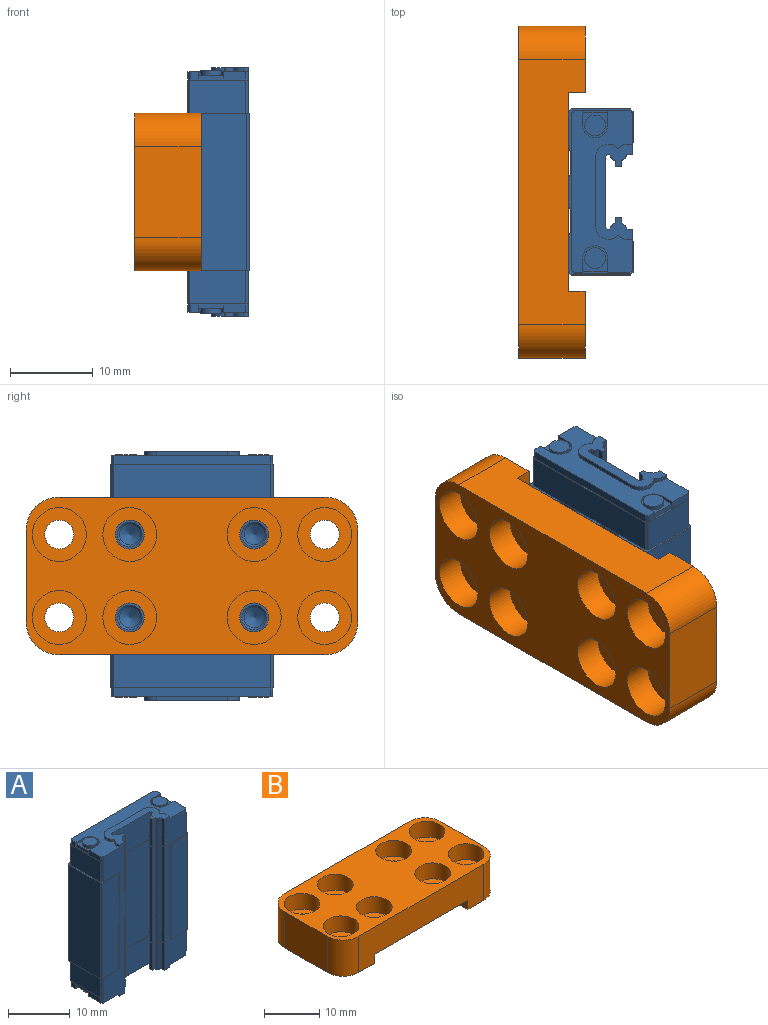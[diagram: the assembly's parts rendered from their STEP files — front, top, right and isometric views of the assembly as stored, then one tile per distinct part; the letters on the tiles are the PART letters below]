
ASSEMBLY  parts=2 mates=1
PART A: 240 faces, bbox 20x7.8x30 mm
  f0: cone r=0mm half-angle=60deg, axis (0,1,0), area 5.5mm2, adj f8
  f1: cone r=0mm half-angle=60deg, axis (0,1,0), area 5.5mm2, adj f9
  f2: cone r=0mm half-angle=60deg, axis (0,1,0), area 5.5mm2, adj f10
  f3: cone r=0mm half-angle=60deg, axis (0,1,0), area 5.5mm2, adj f11
  f4: plane 2.5x2.5mm, normal (0,0,1), area 4.9mm2, adj f12
  f5: plane 2.5x2.5mm, normal (0,0,1), area 4.9mm2, adj f13
  f6: plane 19x0.26mm, normal (1,0,0), area 4.9mm2, adj f21,f22,f91,f92
  f7: plane 19x0.26mm, normal (-1,0,0), area 4.9mm2, adj f24,f25,f91,f92
  f8: cylinder r=1.23mm len=5.73mm, axis (0,-1,0), area 44.3mm2, adj f0,f31
  f9: cylinder r=1.23mm len=5.73mm, axis (0,-1,0), area 44.3mm2, adj f1,f32
  f10: cylinder r=1.23mm len=5.73mm, axis (0,-1,0), area 44.3mm2, adj f2,f33
  f11: cylinder r=1.23mm len=5.73mm, axis (0,-1,0), area 44.3mm2, adj f3,f34
  f12: cylinder r=1.25mm len=2.5mm, axis (0,0,-1), area 3.9mm2, adj f4,f35
  f13: cylinder r=1.25mm len=2.5mm, axis (0,0,-1), area 3.9mm2, adj f5,f37
  f14: plane 2.5x2.5mm, normal (0,0,-1), area 4.9mm2, adj f89
  f15: plane 2.5x2.5mm, normal (0,0,-1), area 4.9mm2, adj f90
  f16: cylinder r=1.1mm len=19mm, axis (0,0,-1), area 13.7mm2, adj f17,f88,f91,f92
  f17: plane 19x0.66mm, normal (0,-1,0), area 12.4mm2, adj f16,f18,f91,f92
  f18: plane 19x0.7mm, normal (1,0,0), area 13.3mm2, adj f17,f19,f91,f92
  f19: plane 19x0.66mm, normal (0,1,0), area 12.4mm2, adj f18,f20,f91,f92
  f20: cylinder r=1.1mm len=19mm, axis (0,0,-1), area 13.7mm2, adj f19,f21,f91,f92
  f21: plane 19x0.28mm, normal (0.5,0.87,0), area 6.1mm2, adj f6,f20,f91,f92
  f22: plane 19x0.2mm, normal (0.71,-0.71,0), area 5.4mm2, adj f6,f23,f91,f92
  f23: plane 19x8.6mm, normal (0,-1,0), area 163.4mm2, adj f22,f24,f91,f92
  f24: plane 19x0.2mm, normal (-0.71,-0.71,0), area 5.4mm2, adj f7,f23,f91,f92
  f25: plane 19x0.28mm, normal (-0.5,0.87,0), area 6.1mm2, adj f7,f26,f91,f92
  f26: cylinder r=1.1mm len=19mm, axis (0,0,-1), area 13.7mm2, adj f25,f27,f91,f92
  f27: plane 19x0.66mm, normal (0,1,0), area 12.4mm2, adj f26,f28,f91,f92
  f28: plane 19x0.7mm, normal (-1,0,0), area 13.3mm2, adj f27,f29,f91,f92
  f29: plane 19x0.66mm, normal (0,-1,0), area 12.4mm2, adj f28,f30,f91,f92
  f30: cylinder r=1.1mm len=19mm, axis (0,0,-1), area 13.7mm2, adj f29,f91,f92,f93
  f31: cone r=0mm half-angle=45deg, axis (0,1,0), area 3.3mm2, adj f8,f106
  f32: cone r=0mm half-angle=45deg, axis (0,1,0), area 3.3mm2, adj f9,f106
  f33: cone r=0mm half-angle=45deg, axis (0,1,0), area 3.3mm2, adj f10,f114
  f34: cone r=0mm half-angle=45deg, axis (0,1,0), area 3.3mm2, adj f11,f114
  f35: plane 3.05x3mm, normal (0,0,1), area 3.3mm2, adj f12,f36,f123,f124,f125
  f36: plane 3x0.6mm, normal (1,0,0), area 1.8mm2, adj f35,f121,f123,f125
  f37: plane 3.05x3mm, normal (0,0,1), area 3.3mm2, adj f13,f38,f131,f132,f133,f134
  f38: plane 3x0.6mm, normal (-1,0,0), area 1.8mm2, adj f37,f121,f131,f134
  f39: plane 5.45x0.26mm, normal (1,0,0), area 1.4mm2, adj f142,f143,f159,f187
  f40: plane 5.45x0.26mm, normal (-1,0,0), area 1.4mm2, adj f145,f146,f159,f187
  f41: cylinder r=0.1mm len=0.5mm, axis (0,0,1), area 0.1mm2, adj f152,f153,f185,f187
  f42: plane 0.5x0.15mm, normal (1,0,0), area 0.1mm2, adj f153,f154,f185,f187
  f43: plane 0.5x0.15mm, normal (-1,0,0), area 0.1mm2, adj f156,f157,f185,f187
  f44: cylinder r=0.1mm len=0.5mm, axis (0,0,1), area 0mm2, adj f45,f157,f185,f187
  f45: cylinder r=0.1mm len=0.5mm, axis (0,0,1), area 0mm2, adj f44,f158,f185,f187
  f46: plane 0.71x0.05mm, normal (1,0,0), area 0mm2, adj f47,f92,f159,f215
  f47: plane 0.25x0.12mm, normal (0.45,-0.89,0), area 0mm2, adj f46,f48,f92,f159
  f48: cylinder r=1.05mm len=0.57mm, axis (0,0,-1), area 0mm2, adj f47,f49,f92,f159
  f49: plane 0.64x0.05mm, normal (0,-1,0), area 0mm2, adj f48,f50,f92,f159
  f50: plane 0.6x0.05mm, normal (1,0,0), area 0mm2, adj f49,f51,f92,f159
  f51: plane 0.64x0.05mm, normal (0,1,0), area 0mm2, adj f50,f52,f92,f159
  f52: cylinder r=1.05mm len=0.57mm, axis (0,0,-1), area 0mm2, adj f51,f53,f92,f159
  f53: plane 0.25x0.12mm, normal (0.45,0.89,0), area 0mm2, adj f52,f54,f92,f159
  f54: plane 0.36x0.05mm, normal (1,0,0), area 0mm2, adj f53,f55,f92,f159
  f55: plane 0.2x0.2mm, normal (0.71,-0.71,0), area 0mm2, adj f54,f56,f92,f159
  f56: plane 8.7x0.05mm, normal (0,-1,0), area 0.4mm2, adj f55,f57,f92,f159
  f57: plane 0.2x0.2mm, normal (-0.71,-0.71,0), area 0mm2, adj f56,f58,f92,f159
  f58: plane 0.36x0.05mm, normal (-1,0,0), area 0mm2, adj f57,f59,f92,f159
  f59: plane 0.25x0.12mm, normal (-0.45,0.89,0), area 0mm2, adj f58,f60,f92,f159
  f60: cylinder r=1.05mm len=0.57mm, axis (0,0,-1), area 0mm2, adj f59,f61,f92,f159
  f61: plane 0.64x0.05mm, normal (0,1,0), area 0mm2, adj f60,f62,f92,f159
  f62: plane 0.6x0.05mm, normal (-1,0,0), area 0mm2, adj f61,f63,f92,f159
  f63: plane 0.64x0.05mm, normal (0,-1,0), area 0mm2, adj f62,f64,f92,f159
  f64: cylinder r=1.05mm len=0.57mm, axis (0,0,-1), area 0mm2, adj f63,f65,f92,f159
  f65: plane 0.25x0.12mm, normal (-0.45,-0.89,0), area 0mm2, adj f64,f66,f92,f159
  f66: plane 0.71x0.05mm, normal (-1,0,0), area 0mm2, adj f65,f92,f159,f232
  f67: plane 0.71x0.05mm, normal (-1,0,0), area 0mm2, adj f68,f91,f163,f232
  f68: plane 0.25x0.12mm, normal (-0.45,-0.89,0), area 0mm2, adj f67,f69,f91,f163
  f69: cylinder r=1.05mm len=0.57mm, axis (0,0,1), area 0mm2, adj f68,f70,f91,f163
  f70: plane 0.64x0.05mm, normal (0,-1,0), area 0mm2, adj f69,f71,f91,f163
  f71: plane 0.6x0.05mm, normal (-1,0,0), area 0mm2, adj f70,f72,f91,f163
  f72: plane 0.64x0.05mm, normal (0,1,0), area 0mm2, adj f71,f73,f91,f163
  f73: cylinder r=1.05mm len=0.57mm, axis (0,0,1), area 0mm2, adj f72,f74,f91,f163
  f74: plane 0.25x0.12mm, normal (-0.45,0.89,0), area 0mm2, adj f73,f75,f91,f163
  f75: plane 0.36x0.05mm, normal (-1,0,0), area 0mm2, adj f74,f76,f91,f163
  f76: plane 0.2x0.2mm, normal (-0.71,-0.71,0), area 0mm2, adj f75,f77,f91,f163
  f77: plane 8.7x0.05mm, normal (0,-1,0), area 0.4mm2, adj f76,f78,f91,f163
  f78: plane 0.2x0.2mm, normal (0.71,-0.71,0), area 0mm2, adj f77,f79,f91,f163
  f79: plane 0.36x0.05mm, normal (1,0,0), area 0mm2, adj f78,f80,f91,f163
  f80: plane 0.25x0.12mm, normal (0.45,0.89,0), area 0mm2, adj f79,f81,f91,f163
  f81: cylinder r=1.05mm len=0.57mm, axis (0,0,1), area 0mm2, adj f80,f82,f91,f163
  f82: plane 0.64x0.05mm, normal (0,1,0), area 0mm2, adj f81,f83,f91,f163
  f83: plane 0.6x0.05mm, normal (1,0,0), area 0mm2, adj f82,f84,f91,f163
  f84: plane 0.64x0.05mm, normal (0,-1,0), area 0mm2, adj f83,f85,f91,f163
  f85: cylinder r=1.05mm len=0.57mm, axis (0,0,1), area 0mm2, adj f84,f86,f91,f163
  f86: plane 0.25x0.12mm, normal (0.45,-0.89,0), area 0mm2, adj f85,f87,f91,f163
  f87: plane 0.71x0.05mm, normal (1,0,0), area 0mm2, adj f86,f91,f163,f215
  f88: plane 19x0.28mm, normal (0.5,-0.87,0), area 6.1mm2, adj f16,f91,f92,f168
  f89: cylinder r=1.25mm len=2.5mm, axis (0,0,-1), area 3.9mm2, adj f14,f173
  f90: cylinder r=1.25mm len=2.5mm, axis (0,0,-1), area 3.9mm2, adj f15,f175
  f91: plane 9.1x3.25mm, normal (0,0,-1), area 1mm2, adj f6,f7,f16,f17,f18,f19,f20,f21
  f92: plane 9.1x3.25mm, normal (0,0,1), area 1mm2, adj f6,f7,f16,f17,f18,f19,f20,f21
  f93: plane 19x0.28mm, normal (-0.5,-0.87,0), area 6.1mm2, adj f30,f91,f92,f178
  f94: plane 4x0.3mm, normal (0.71,0.71,0), area 1.7mm2, adj f95,f98,f177,f180
  f95: plane 19x4mm, normal (0,1,0), area 76mm2, adj f94,f96,f177,f180
  f96: plane 4x0.3mm, normal (-0.71,0.71,0), area 1.7mm2, adj f95,f97,f177,f180
  f97: plane 6.8x4mm, normal (-1,0,0), area 27.2mm2, adj f96,f167,f177,f180
  f98: plane 6.8x4mm, normal (1,0,0), area 27.2mm2, adj f94,f177,f179,f180
  f99: plane 4x0.3mm, normal (-0.71,0.71,0), area 1.7mm2, adj f100,f119,f121,f182
  f100: plane 19x4mm, normal (0,1,0), area 76mm2, adj f99,f101,f121,f182
  f101: plane 4x0.3mm, normal (0.71,0.71,0), area 1.7mm2, adj f100,f120,f121,f182
  f102: plane 19x3.73mm, normal (0,-1,0), area 70.8mm2, adj f103,f180,f181,f182
  f103: plane 19x0.3mm, normal (0.71,-0.71,0), area 8.1mm2, adj f102,f104,f180,f182
  f104: plane 19x7.2mm, normal (1,0,0), area 136.8mm2, adj f103,f105,f180,f182
  f105: plane 19x0.3mm, normal (0.71,0.71,0), area 8.1mm2, adj f104,f106,f180,f182
  f106: plane 19x4.4mm, normal (0,1,0), area 69.5mm2, adj f31,f32,f105,f107,f180,f182
  f107: plane 19x0.4mm, normal (-0.53,0.85,0), area 9mm2, adj f106,f108,f180,f182
  f108: plane 19x2.8mm, normal (0,1,0), area 53.2mm2, adj f107,f109,f180,f182
  f109: plane 19x0.4mm, normal (0.53,0.85,0), area 9mm2, adj f108,f110,f180,f182
  f110: plane 19x3.4mm, normal (0,1,0), area 64.6mm2, adj f109,f111,f180,f182
  f111: plane 19x0.4mm, normal (-0.53,0.85,0), area 9mm2, adj f110,f112,f180,f182
  f112: plane 19x2.8mm, normal (0,1,0), area 53.2mm2, adj f111,f113,f180,f182
  f113: plane 19x0.4mm, normal (0.53,0.85,0), area 9mm2, adj f112,f114,f180,f182
  f114: plane 19x4.4mm, normal (0,1,0), area 69.5mm2, adj f33,f34,f113,f115,f180,f182
  f115: plane 19x0.3mm, normal (-0.71,0.71,0), area 8.1mm2, adj f114,f116,f180,f182
  f116: plane 19x7.2mm, normal (-1,0,0), area 136.8mm2, adj f115,f117,f180,f182
  f117: plane 19x0.3mm, normal (-0.71,-0.71,0), area 8.1mm2, adj f116,f118,f180,f182
  f118: plane 19x3.73mm, normal (0,-1,0), area 70.8mm2, adj f117,f166,f180,f182
  f119: plane 6.8x4mm, normal (-1,0,0), area 27.2mm2, adj f99,f121,f172,f182
  f120: plane 6.8x4mm, normal (1,0,0), area 27.2mm2, adj f101,f121,f182,f183
  f121: plane 19.6x7.4mm, normal (0,0,1), area 3.9mm2, adj f36,f38,f99,f100,f101,f119,f120,f122
  f122: plane 2.7x1mm, normal (1,0,0), area 2.7mm2, adj f121,f123,f184,f185
  f123: plane 1.75x1mm, normal (0,1,0), area 0.8mm2, adj f35,f36,f121,f122,f124,f185
  f124: cylinder r=1.5mm len=3mm, axis (0,0,1), area 1.9mm2, adj f35,f123,f125,f185
  f125: plane 1.75x1mm, normal (0,-1,0), area 0.8mm2, adj f35,f36,f121,f124,f126,f185
  f126: plane 1x1mm, normal (1,0,0), area 1mm2, adj f121,f125,f127,f185
  f127: plane 1x0.3mm, normal (0.71,0.71,0), area 0.4mm2, adj f121,f126,f128,f185
  f128: plane 18.9x1mm, normal (0,1,0), area 18.9mm2, adj f121,f127,f129,f185
  f129: plane 1x0.3mm, normal (-0.71,0.71,0), area 0.4mm2, adj f121,f128,f130,f185
  f130: plane 1x1mm, normal (-1,0,0), area 1mm2, adj f121,f129,f131,f185
  f131: plane 1.75x1mm, normal (0,-1,0), area 0.8mm2, adj f37,f38,f121,f130,f132,f185
  f132: cylinder r=1.5mm len=1.5mm, axis (0,0,1), area 0.9mm2, adj f37,f131,f133,f185
  f133: cylinder r=1.5mm len=1.5mm, axis (0,0,1), area 0.9mm2, adj f37,f132,f134,f185
  f134: plane 1.75x1mm, normal (0,1,0), area 0.8mm2, adj f37,f38,f121,f133,f135,f185
  f135: plane 2.7x1mm, normal (-1,0,0), area 2.7mm2, adj f121,f134,f171,f185
  f136: plane 5.45x0.28mm, normal (0.5,-0.87,0), area 1.8mm2, adj f137,f159,f169,f187
  f137: cylinder r=1.1mm len=5.45mm, axis (0,0,-1), area 3.9mm2, adj f136,f138,f159,f187
  f138: plane 5.45x0.66mm, normal (0,-1,0), area 3.6mm2, adj f137,f139,f159,f187
  f139: plane 5.45x0.7mm, normal (1,0,0), area 3.8mm2, adj f138,f140,f159,f187
  f140: plane 5.45x0.66mm, normal (0,1,0), area 3.6mm2, adj f139,f141,f159,f187
  f141: cylinder r=1.1mm len=5.45mm, axis (0,0,-1), area 3.9mm2, adj f140,f142,f159,f187
  f142: plane 5.45x0.28mm, normal (0.5,0.87,0), area 1.8mm2, adj f39,f141,f159,f187
  f143: plane 5.45x0.2mm, normal (0.71,-0.71,0), area 1.5mm2, adj f39,f144,f159,f187
  f144: plane 8.6x5.45mm, normal (0,-1,0), area 46.9mm2, adj f143,f145,f159,f187
  f145: plane 5.45x0.2mm, normal (-0.71,-0.71,0), area 1.5mm2, adj f40,f144,f159,f187
  f146: plane 5.45x0.28mm, normal (-0.5,0.87,0), area 1.8mm2, adj f40,f147,f159,f187
  f147: cylinder r=1.1mm len=5.45mm, axis (0,0,-1), area 3.9mm2, adj f146,f148,f159,f187
  f148: plane 5.45x0.66mm, normal (0,1,0), area 3.6mm2, adj f147,f149,f159,f187
  f149: plane 5.45x0.7mm, normal (-1,0,0), area 3.8mm2, adj f148,f150,f159,f187
  f150: plane 5.45x0.66mm, normal (0,-1,0), area 3.6mm2, adj f149,f151,f159,f187
  f151: cylinder r=1.1mm len=5.45mm, axis (0,0,-1), area 3.9mm2, adj f150,f159,f160,f187
  f152: cylinder r=1.3mm len=1.01mm, axis (0,0,1), area 0.6mm2, adj f41,f185,f186,f187
  f153: cylinder r=1.3mm len=1.01mm, axis (0,0,1), area 0.6mm2, adj f41,f42,f185,f187
  f154: cylinder r=1.5mm len=1.5mm, axis (0,0,1), area 1.2mm2, adj f42,f155,f185,f187
  f155: plane 8.46x0.5mm, normal (0,1,0), area 4.2mm2, adj f154,f156,f185,f187
  f156: cylinder r=1.5mm len=1.5mm, axis (0,0,1), area 1.2mm2, adj f43,f155,f185,f187
  f157: cylinder r=1.3mm len=1.01mm, axis (0,0,1), area 0.6mm2, adj f43,f44,f185,f187
  f158: cylinder r=1.3mm len=1.01mm, axis (0,0,1), area 0.6mm2, adj f45,f170,f185,f187
  f159: plane 9.1x3.25mm, normal (0,0,-1), area 1mm2, adj f39,f40,f46,f47,f48,f49,f50,f51
  f160: plane 5.45x0.28mm, normal (-0.5,-0.87,0), area 1.8mm2, adj f151,f159,f187,f188
  f161: plane 5.45x0.26mm, normal (-1,0,0), area 1.4mm2, adj f163,f198,f199,f234
  f162: plane 5.45x0.26mm, normal (1,0,0), area 1.4mm2, adj f163,f201,f202,f234
  f163: plane 9.1x3.25mm, normal (0,0,1), area 1mm2, adj f67,f68,f69,f70,f71,f72,f73,f74
  f164: plane 0.5x0.15mm, normal (-1,0,0), area 0.1mm2, adj f211,f212,f234,f236
  f165: cylinder r=0.1mm len=0.5mm, axis (0,0,-1), area 0.1mm2, adj f212,f213,f234,f236
  f166: plane 19x0.21mm, normal (0.42,-0.91,0), area 4.5mm2, adj f118,f180,f182,f215
  f167: plane 4x0.3mm, normal (-0.71,-0.71,0), area 1.7mm2, adj f97,f177,f180,f215
  f168: plane 19x0.66mm, normal (1,0,0), area 12.5mm2, adj f88,f91,f92,f215
  f169: plane 5.45x0.66mm, normal (1,0,0), area 3.6mm2, adj f136,f159,f187,f215
  f170: plane 0.62x0.5mm, normal (-1,0,0), area 0.3mm2, adj f158,f185,f187,f215
  f171: plane 1x0.3mm, normal (-0.71,-0.71,0), area 0.4mm2, adj f121,f135,f185,f215
  f172: plane 4x0.3mm, normal (-0.71,-0.71,0), area 1.7mm2, adj f119,f121,f182,f215
  f173: plane 3.05x3mm, normal (0,0,-1), area 3.3mm2, adj f89,f174,f218,f219,f220
  f174: plane 3x0.6mm, normal (-1,0,0), area 1.8mm2, adj f173,f177,f218,f220
  f175: plane 3.05x3mm, normal (0,0,-1), area 3.3mm2, adj f90,f176,f226,f227,f228,f229
  f176: plane 3x0.6mm, normal (1,0,0), area 1.8mm2, adj f175,f177,f226,f229
  f177: plane 19.6x7.4mm, normal (0,0,-1), area 3.9mm2, adj f94,f95,f96,f97,f98,f167,f174,f176
  f178: plane 19x0.66mm, normal (-1,0,0), area 12.5mm2, adj f91,f92,f93,f232
  f179: plane 4x0.3mm, normal (0.71,-0.71,0), area 1.7mm2, adj f98,f177,f180,f232
  f180: plane 20x7.8mm, normal (0,0,-1), area 8.2mm2, adj f94,f95,f96,f97,f98,f102,f103,f104
  f181: plane 19x0.21mm, normal (-0.42,-0.91,0), area 4.5mm2, adj f102,f180,f182,f232
  f182: plane 20x7.8mm, normal (0,0,1), area 8.2mm2, adj f99,f100,f101,f102,f103,f104,f105,f106
  f183: plane 4x0.3mm, normal (0.71,-0.71,0), area 1.7mm2, adj f120,f121,f182,f232
  f184: plane 1x0.3mm, normal (0.71,-0.71,0), area 0.4mm2, adj f121,f122,f185,f232
  f185: plane 19.5x7.3mm, normal (0,0,1), area 75.5mm2, adj f41,f42,f43,f44,f45,f122,f123,f124
  f186: plane 0.62x0.5mm, normal (1,0,0), area 0.3mm2, adj f152,f185,f187,f232
  f187: plane 11.46x4.43mm, normal (0,0,1), area 23.6mm2, adj f39,f40,f41,f42,f43,f44,f45,f136
  f188: plane 5.45x0.66mm, normal (-1,0,0), area 3.6mm2, adj f159,f160,f187,f232
  f189: plane 5.45x0.28mm, normal (0.5,-0.87,0), area 1.8mm2, adj f163,f190,f207,f234
  f190: plane 5.45x0.66mm, normal (1,0,0), area 3.6mm2, adj f163,f189,f215,f234
  f191: plane 5.45x0.66mm, normal (-1,0,0), area 3.6mm2, adj f163,f192,f232,f234
  f192: plane 5.45x0.28mm, normal (-0.5,-0.87,0), area 1.8mm2, adj f163,f191,f193,f234
  f193: cylinder r=1.1mm len=5.45mm, axis (0,0,-1), area 3.9mm2, adj f163,f192,f194,f234
  f194: plane 5.45x0.66mm, normal (0,-1,0), area 3.6mm2, adj f163,f193,f195,f234
  f195: plane 5.45x0.7mm, normal (-1,0,0), area 3.8mm2, adj f163,f194,f196,f234
  f196: plane 5.45x0.66mm, normal (0,1,0), area 3.6mm2, adj f163,f195,f197,f234
  f197: cylinder r=1.1mm len=5.45mm, axis (0,0,-1), area 3.9mm2, adj f163,f196,f198,f234
  f198: plane 5.45x0.28mm, normal (-0.5,0.87,0), area 1.8mm2, adj f161,f163,f197,f234
  f199: plane 5.45x0.2mm, normal (-0.71,-0.71,0), area 1.5mm2, adj f161,f163,f200,f234
  f200: plane 8.6x5.45mm, normal (0,-1,0), area 46.9mm2, adj f163,f199,f201,f234
  f201: plane 5.45x0.2mm, normal (0.71,-0.71,0), area 1.5mm2, adj f162,f163,f200,f234
  f202: plane 5.45x0.28mm, normal (0.5,0.87,0), area 1.8mm2, adj f162,f163,f203,f234
  f203: cylinder r=1.1mm len=5.45mm, axis (0,0,-1), area 3.9mm2, adj f163,f202,f204,f234
  f204: plane 5.45x0.66mm, normal (0,1,0), area 3.6mm2, adj f163,f203,f205,f234
  f205: plane 5.45x0.7mm, normal (1,0,0), area 3.8mm2, adj f163,f204,f206,f234
  f206: plane 5.45x0.66mm, normal (0,-1,0), area 3.6mm2, adj f163,f205,f207,f234
  f207: cylinder r=1.1mm len=5.45mm, axis (0,0,-1), area 3.9mm2, adj f163,f189,f206,f234
  f208: plane 0.62x0.5mm, normal (1,0,0), area 0.3mm2, adj f232,f233,f234,f236
  f209: cylinder r=1.5mm len=1.5mm, axis (0,0,-1), area 1.2mm2, adj f210,f234,f235,f236
  f210: plane 8.46x0.5mm, normal (0,1,0), area 4.2mm2, adj f209,f211,f234,f236
  f211: cylinder r=1.5mm len=1.5mm, axis (0,0,-1), area 1.2mm2, adj f164,f210,f234,f236
  f212: cylinder r=1.3mm len=1.01mm, axis (0,0,-1), area 0.6mm2, adj f164,f165,f234,f236
  f213: cylinder r=1.3mm len=1.01mm, axis (0,0,-1), area 0.6mm2, adj f165,f214,f234,f236
  f214: plane 0.62x0.5mm, normal (-1,0,0), area 0.3mm2, adj f213,f215,f234,f236
  f215: plane 30x5mm, normal (0,-1,0), area 75mm2, adj f46,f87,f91,f92,f121,f159,f163,f166
  f216: plane 1x0.3mm, normal (-0.71,-0.71,0), area 0.4mm2, adj f177,f215,f217,f236
  f217: plane 2.7x1mm, normal (-1,0,0), area 2.7mm2, adj f177,f216,f218,f236
  f218: plane 1.75x1mm, normal (0,1,0), area 0.8mm2, adj f173,f174,f177,f217,f219,f236
  f219: cylinder r=1.5mm len=3mm, axis (0,0,-1), area 1.9mm2, adj f173,f218,f220,f236
  f220: plane 1.75x1mm, normal (0,-1,0), area 0.8mm2, adj f173,f174,f177,f219,f221,f236
  f221: plane 1x1mm, normal (-1,0,0), area 1mm2, adj f177,f220,f222,f236
  f222: plane 1x0.3mm, normal (-0.71,0.71,0), area 0.4mm2, adj f177,f221,f223,f236
  f223: plane 18.9x1mm, normal (0,1,0), area 18.9mm2, adj f177,f222,f224,f236
  f224: plane 1x0.3mm, normal (0.71,0.71,0), area 0.4mm2, adj f177,f223,f225,f236
  f225: plane 1x1mm, normal (1,0,0), area 1mm2, adj f177,f224,f226,f236
  f226: plane 1.75x1mm, normal (0,-1,0), area 0.8mm2, adj f175,f176,f177,f225,f227,f236
  f227: cylinder r=1.5mm len=1.5mm, axis (0,0,-1), area 0.9mm2, adj f175,f226,f228,f236
  f228: cylinder r=1.5mm len=1.5mm, axis (0,0,-1), area 0.9mm2, adj f175,f227,f229,f236
  f229: plane 1.75x1mm, normal (0,1,0), area 0.8mm2, adj f175,f176,f177,f228,f230,f236
  f230: plane 2.7x1mm, normal (1,0,0), area 2.7mm2, adj f177,f229,f231,f236
  f231: plane 1x0.3mm, normal (0.71,-0.71,0), area 0.4mm2, adj f177,f230,f232,f236
  f232: plane 30x5mm, normal (0,-1,0), area 75mm2, adj f66,f67,f91,f92,f121,f159,f163,f177
  f233: cylinder r=1.3mm len=1.01mm, axis (0,0,-1), area 0.6mm2, adj f208,f234,f236,f237
  f234: plane 11.46x4.43mm, normal (0,0,-1), area 23.6mm2, adj f161,f162,f164,f165,f189,f190,f191,f192
  f235: plane 0.5x0.15mm, normal (1,0,0), area 0.1mm2, adj f209,f234,f236,f238
  f236: plane 19.5x7.3mm, normal (0,0,-1), area 75.5mm2, adj f164,f165,f208,f209,f210,f211,f212,f213
  f237: cylinder r=0.1mm len=0.5mm, axis (0,0,-1), area 0mm2, adj f233,f234,f236,f239
  f238: cylinder r=1.3mm len=1.01mm, axis (0,0,-1), area 0.6mm2, adj f234,f235,f236,f239
  f239: cylinder r=0.1mm len=0.5mm, axis (0,0,-1), area 0mm2, adj f234,f236,f237,f238
PART B: 38 faces, bbox 40x19x8 mm
  f0: cylinder r=1.75mm len=3.5mm, axis (0,0,-1), area 27.5mm2, adj f19,f23
  f1: cylinder r=1.75mm len=3.5mm, axis (0,0,-1), area 27.5mm2, adj f19,f33
  f2: cylinder r=1.75mm len=3.5mm, axis (0,0,-1), area 27.5mm2, adj f19,f28
  f3: cylinder r=1.75mm len=3.5mm, axis (0,0,-1), area 27.5mm2, adj f19,f36
  f4: cylinder r=1.75mm len=4.5mm, axis (0,0,-1), area 49.5mm2, adj f8,f31
  f5: cylinder r=1.75mm len=4.5mm, axis (0,0,-1), area 49.5mm2, adj f8,f35
  f6: cylinder r=1.75mm len=4.5mm, axis (0,0,-1), area 49.5mm2, adj f18,f24
  f7: cylinder r=1.75mm len=4.5mm, axis (0,0,-1), area 49.5mm2, adj f18,f26
  f8: plane 19x8mm, normal (0,0,-1), area 125.9mm2, adj f4,f5,f9,f13,f14,f15,f16,f21
  f9: plane 32x8mm, normal (0,1,0), area 208mm2, adj f8,f10,f16,f17,f18,f19,f20,f21
  f10: cylinder r=4mm len=8mm, axis (0,0,-1), area 50.3mm2, adj f9,f11,f17,f18
  f11: plane 11x8mm, normal (-1,0,0), area 88mm2, adj f10,f12,f17,f18
  f12: cylinder r=4mm len=8mm, axis (0,0,-1), area 50.3mm2, adj f11,f13,f17,f18
  f13: plane 32x8mm, normal (0,-1,0), area 208mm2, adj f8,f12,f14,f17,f18,f19,f20,f21
  f14: cylinder r=4mm len=8mm, axis (0,0,-1), area 50.3mm2, adj f8,f13,f15,f17
  f15: plane 11x8mm, normal (1,0,0), area 88mm2, adj f8,f14,f16,f17
  f16: cylinder r=4mm len=8mm, axis (0,0,-1), area 50.3mm2, adj f8,f9,f15,f17
  f17: plane 40x19mm, normal (0,0,1), area 480.8mm2, adj f9,f10,f11,f12,f13,f14,f15,f16
  f18: plane 19x8mm, normal (0,0,-1), area 125.9mm2, adj f6,f7,f9,f10,f11,f12,f13,f20
  f19: plane 24x19mm, normal (0,0,-1), area 417.5mm2, adj f0,f1,f2,f3,f9,f13,f20,f21
  f20: plane 19x2mm, normal (1,0,0), area 38mm2, adj f9,f13,f18,f19
  f21: plane 19x2mm, normal (-1,0,0), area 38mm2, adj f8,f9,f13,f19
  f22: cylinder r=3.25mm len=6.5mm, axis (0,0,1), area 71.5mm2, adj f17,f23
  f23: plane 6.5x6.5mm, normal (0,0,1), area 23.6mm2, adj f0,f22
  f24: plane 6.5x6.5mm, normal (0,0,1), area 23.6mm2, adj f6,f25
  f25: cylinder r=3.25mm len=6.5mm, axis (0,0,1), area 71.5mm2, adj f17,f24
  f26: plane 6.5x6.5mm, normal (0,0,1), area 23.6mm2, adj f7,f27
  f27: cylinder r=3.25mm len=6.5mm, axis (0,0,1), area 71.5mm2, adj f17,f26
  f28: plane 6.5x6.5mm, normal (0,0,1), area 23.6mm2, adj f2,f29
  f29: cylinder r=3.25mm len=6.5mm, axis (0,0,1), area 71.5mm2, adj f17,f28
  f30: cylinder r=3.25mm len=6.5mm, axis (0,0,1), area 71.5mm2, adj f17,f31
  f31: plane 6.5x6.5mm, normal (0,0,1), area 23.6mm2, adj f4,f30
  f32: cylinder r=3.25mm len=6.5mm, axis (0,0,1), area 71.5mm2, adj f17,f33
  f33: plane 6.5x6.5mm, normal (0,0,1), area 23.6mm2, adj f1,f32
  f34: cylinder r=3.25mm len=6.5mm, axis (0,0,1), area 71.5mm2, adj f17,f35
  f35: plane 6.5x6.5mm, normal (0,0,1), area 23.6mm2, adj f5,f34
  f36: plane 6.5x6.5mm, normal (0,0,1), area 23.6mm2, adj f3,f37
  f37: cylinder r=3.25mm len=6.5mm, axis (0,0,1), area 71.5mm2, adj f17,f36
PLACE A rot(axis=(0,0,1),90deg) t=(-33,0,29)mm
PLACE B rot(axis=(0.58,-0.58,-0.58),120deg) t=(-41,0,29)mm
MATE fastened A.f2 <-> B.f0  axis (-1,0,0) through (-43,-7.5,34)mm
